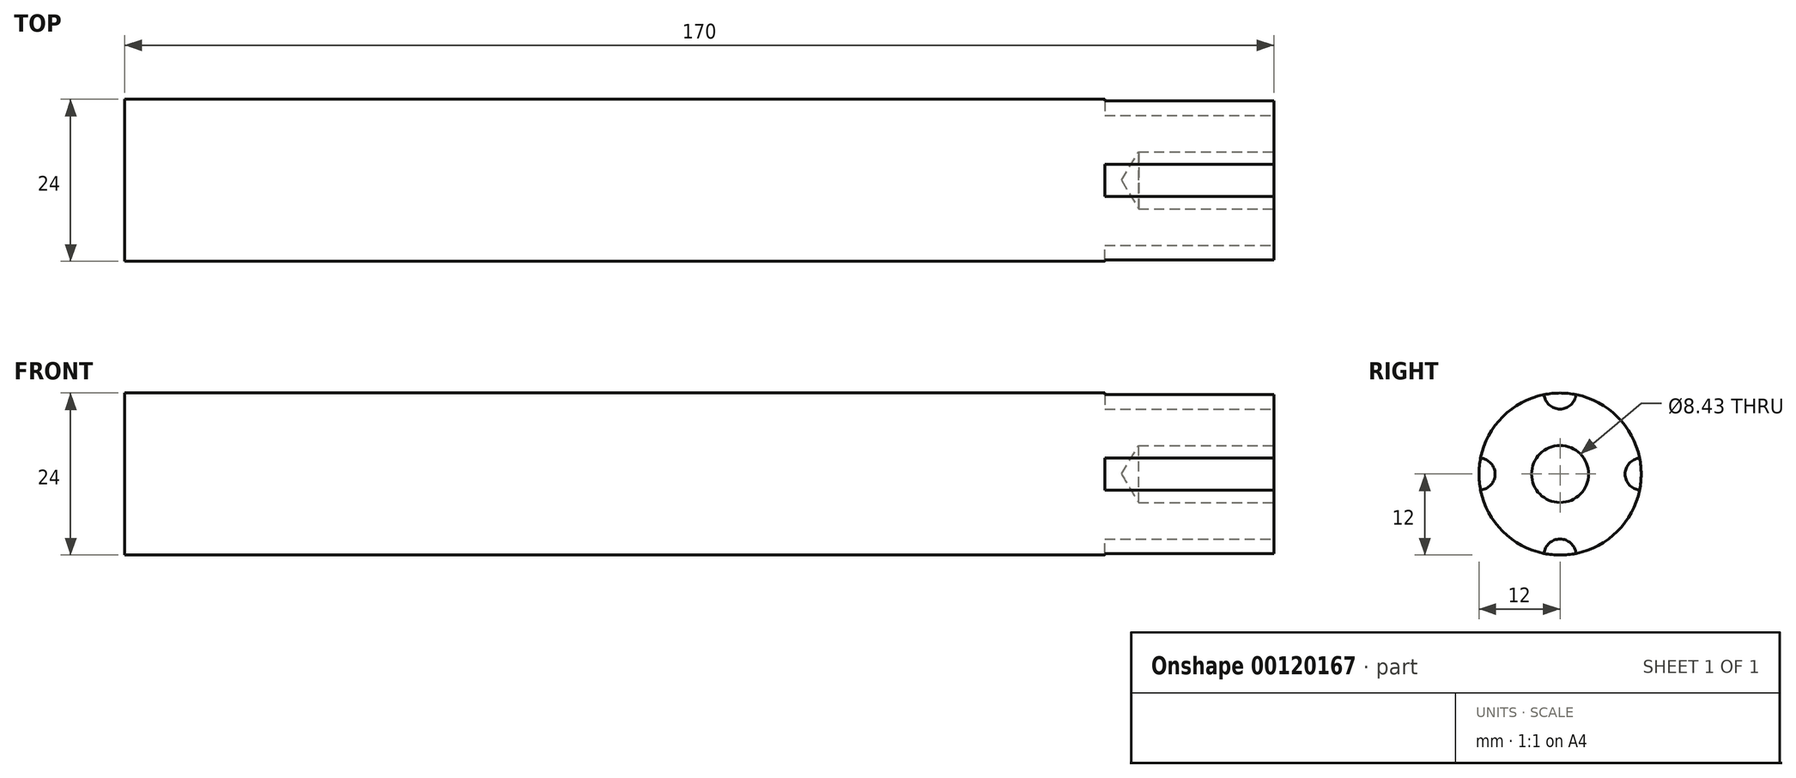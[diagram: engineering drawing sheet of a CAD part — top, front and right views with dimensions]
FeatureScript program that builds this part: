
annotation { "Feature Type Name" : "Feature", "Feature Type Description" : "" }
export const myFeature = defineFeature(function(context is Context, id is Id, definition is map)
    precondition{}
    {
        {
            var Q0;
            Q0=qCreatedBy(makeId("Right.planeOp"),FACE);
            var sketch = newSketch(context, id + "F0", { "sketchPlane" : qUnion([Q0])});
            skCircle(sketch, "E0", {"center": v(0, 0) * mm, "radius": 12 * mm});
            skSolve(sketch);
        }
        {
            var Q0;
            Q0 = qSketchRegion(id + "F0", true);
            extrude(context, id + "F1", {"entities" : qUnion([Q0]), "endBound" : BoundingType.SYMMETRIC, "depth" : 170 * mm});
        }
        {
            var Q0;
            Q0=makeQuery(id+"F1.opExtrude","CAP_FACE",FACE,{"disambiguationData":[OSD([sQuery(id+"F0.wireOp",EDGE,"E0")])],"isStart":false});
            var sketch = newSketch(context, id + "F2", { "sketchPlane" : qUnion([Q0])});
            skArc(sketch, "E1", {"start": v(-2.37, 11.76) * mm, "mid": v(0, 9.62) * mm, "end": v(2.37, 11.76) * mm});
            skArc(sketch, "E2", {"start": v(11.76, 2.37) * mm, "mid": v(9.62, 0) * mm, "end": v(11.76, -2.37) * mm});
            skArc(sketch, "E3", {"start": v(2.37, -11.76) * mm, "mid": v(0, -9.62) * mm, "end": v(-2.37, -11.76) * mm});
            skArc(sketch, "E4", {"start": v(-11.76, -2.37) * mm, "mid": v(-9.62, 0) * mm, "end": v(-11.76, 2.37) * mm});
            skLineSegment(sketch, "E5.bottom", {"start": v(-10.75, -10.75) * mm, "end": v(10.75, -10.75) * mm, "construction": true});
            skLineSegment(sketch, "E5.top", {"start": v(-10.75, 10.75) * mm, "end": v(10.75, 10.75) * mm, "construction": true});
            skLineSegment(sketch, "E5.left", {"start": v(-10.75, -10.75) * mm, "end": v(-10.75, 10.75) * mm, "construction": true});
            skLineSegment(sketch, "E5.right", {"start": v(10.75, -10.75) * mm, "end": v(10.75, 10.75) * mm, "construction": true});
            skPoint(sketch, "E5.middle", {"position": v(0, 0) * mm});
            skArc(sketch, "E6.0", {"start": v(-11.76, 2.37) * mm, "mid": v(-12, 0) * mm, "end": v(-11.76, -2.37) * mm});
            skArc(sketch, "E7.trimOffspring", {"start": v(-2.37, -11.76) * mm, "mid": v(0, -12) * mm, "end": v(2.37, -11.76) * mm});
            skArc(sketch, "E8.trimOffspring", {"start": v(11.76, -2.37) * mm, "mid": v(12, 0) * mm, "end": v(11.76, 2.37) * mm});
            skArc(sketch, "E9.trimOffspring", {"start": v(2.37, 11.76) * mm, "mid": v(0, 12) * mm, "end": v(-2.37, 11.76) * mm});
            skSolve(sketch);
        }
        {
            var Q0;
            Q0 = qSketchRegion(id + "F2", true);
            extrude(context, id + "F3", {"entities" : qUnion([Q0]), "operationType" : NewBodyOperationType.REMOVE, "oppositeDirection" : true, "depth" : 25 * mm});
        }
        {
            var Q0;
            Q0=makeQuery(id+"F1.opExtrude","CAP_FACE",FACE,{"disambiguationData":[OSD([sQuery(id+"F0.wireOp",EDGE,"E0")])],"isStart":false});
            var sketch = newSketch(context, id + "F4", { "sketchPlane" : qUnion([Q0])});
            skPoint(sketch, "E10", {"position": v(0, 0) * mm});
            skSolve(sketch);
        }
        {
            var Q0;
            Q0=sQuery(id+"F4.wireOp",VERTEX,"E10");
            var Q1;
            Q1=makeQuery(id+"F1.opExtrude","SWEPT_BODY",BODY,{"disambiguationData":[OSD([sQuery(id+"F0.wireOp",EDGE,"E0")])]});
            hole(context, id + "F5", {"style" : HoleStyle.SIMPLE, "endStyle" : HoleEndStyle.BLIND, "standardTappedOrClearance" : lookupTablePath({ "standard" : "ANSI", "engagement" : "75%", "pitch" : "24 tpi", "size" : "3/8", "type" : "Tapped" }), "standardBlindInLast" : lookupTablePath({ "standard" : "ANSI", "engagement" : "75%", "pitch" : "24 tpi", "size" : "3/8", "type" : "Tapped" }), "holeDiameter" : 8.43 * mm, "holeDepth" : 20 * mm, "startFromSketch" : true, "locations" : qUnion([Q0]), "scope" : qUnion([Q1]), "majorDiameter" : 9.53 * mm});
        }
    });
